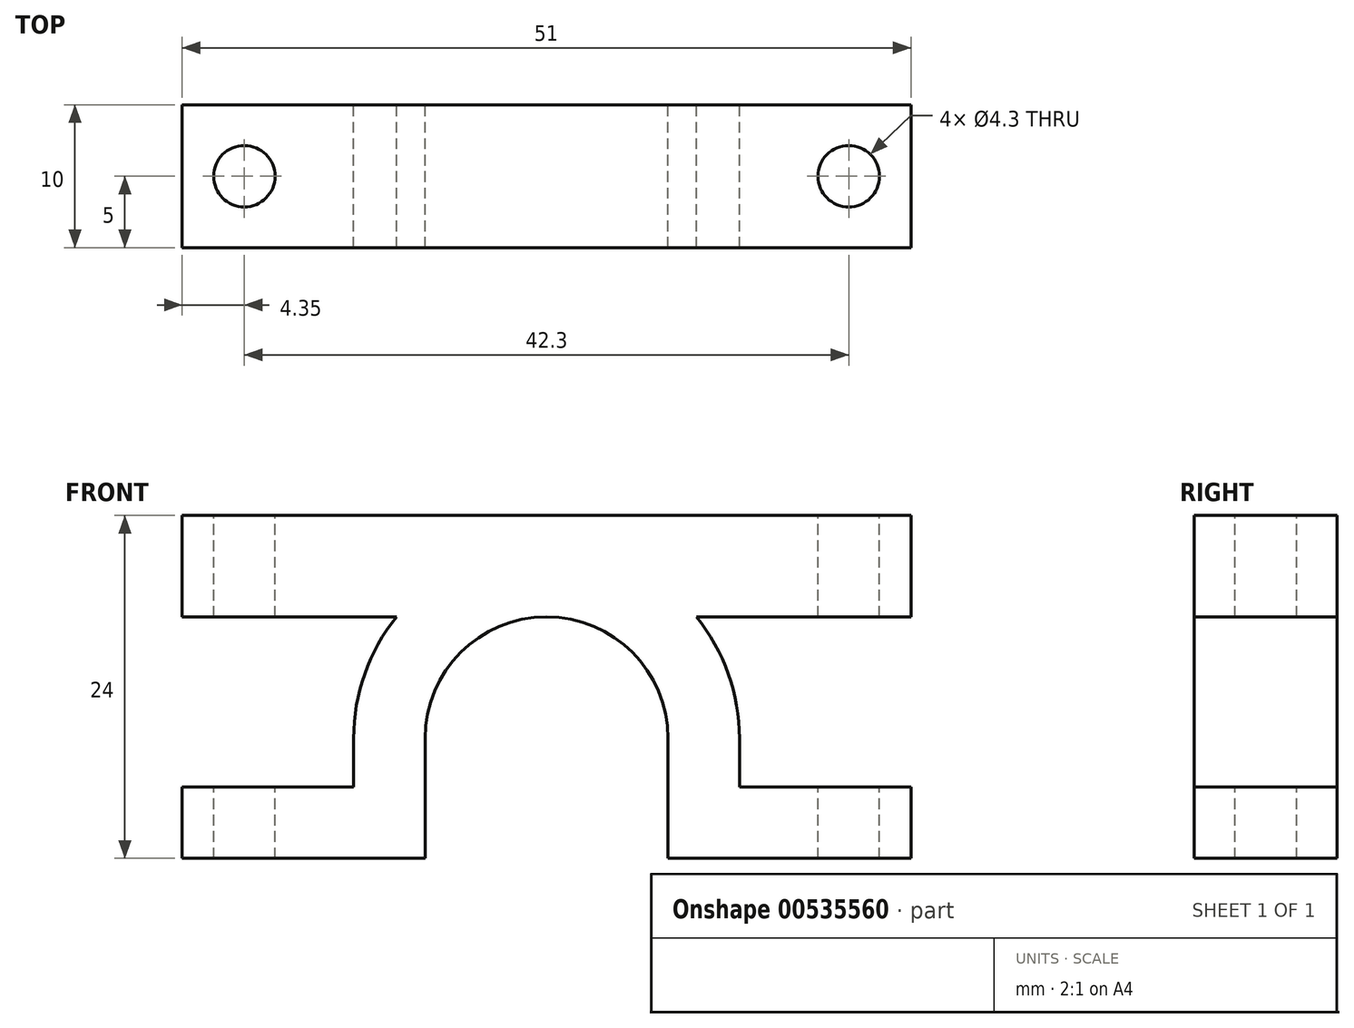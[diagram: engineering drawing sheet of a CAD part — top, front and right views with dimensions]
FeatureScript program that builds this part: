
annotation { "Feature Type Name" : "Feature", "Feature Type Description" : "" }
export const myFeature = defineFeature(function(context is Context, id is Id, definition is map)
    precondition{}
    {
        {
            var Q0;
            Q0=qCreatedBy(makeId("Front.planeOp"),FACE);
            var sketch = newSketch(context, id + "F0", { "sketchPlane" : qUnion([Q0])});
            skCircle(sketch, "E0", {"center": v(0, 0) * mm, "radius": 8.3 * mm});
            skSolve(sketch);
        }
        {
            var Q0;
            Q0=qCreatedBy(makeId("Front.planeOp"),FACE);
            var sketch = newSketch(context, id + "F1", { "sketchPlane" : qUnion([Q0])});
            skLineSegment(sketch, "E1", {"start": v(-25.5, -8.4) * mm, "end": v(-25.5, -3.4) * mm});
            skLineSegment(sketch, "E2", {"start": v(-25.5, -3.4) * mm, "end": v(-13.5, -3.4) * mm});
            skLineSegment(sketch, "E3", {"start": v(-8.5, 0) * mm, "end": v(-8.5, -8.4) * mm});
            skLineSegment(sketch, "E4", {"start": v(-25.5, -8.4) * mm, "end": v(-8.5, -8.4) * mm});
            skLineSegment(sketch, "E5.MirrorCS", {"start": v(8.5, 0) * mm, "end": v(8.5, -8.4) * mm});
            skLineSegment(sketch, "E6.MirrorCS", {"start": v(25.5, -3.4) * mm, "end": v(13.5, -3.4) * mm});
            skLineSegment(sketch, "E7.MirrorCS", {"start": v(25.5, -8.4) * mm, "end": v(25.5, -3.4) * mm});
            skLineSegment(sketch, "E8.MirrorCS", {"start": v(25.5, -8.4) * mm, "end": v(8.5, -8.4) * mm});
            skArc(sketch, "E9", {"start": v(8.5, 0) * mm, "mid": v(0, 8.5) * mm, "end": v(-8.5, 0) * mm});
            skLineSegment(sketch, "E10", {"start": v(-13.5, -3.4) * mm, "end": v(-13.5, 0) * mm});
            skLineSegment(sketch, "E11", {"start": v(13.5, -3.4) * mm, "end": v(13.5, 0) * mm});
            skArc(sketch, "E12", {"start": v(13.5, 0) * mm, "mid": v(0, 13.5) * mm, "end": v(-13.5, 0) * mm});
            skLineSegment(sketch, "E13.bottom", {"start": v(-25.5, 15.6) * mm, "end": v(25.5, 15.6) * mm});
            skLineSegment(sketch, "E13.top", {"start": v(-25.5, 8.5) * mm, "end": v(25.5, 8.5) * mm});
            skLineSegment(sketch, "E13.left", {"start": v(-25.5, 15.6) * mm, "end": v(-25.5, 8.5) * mm});
            skLineSegment(sketch, "E13.right", {"start": v(25.5, 15.6) * mm, "end": v(25.5, 8.5) * mm});
            skPoint(sketch, "E13.middle", {"position": v(0, 12.05) * mm});
            skSolve(sketch);
        }
        {
            var Q0;
            Q0 = qSketchRegion(id + "F1", true);
            extrude(context, id + "F2", {"entities" : qUnion([Q0]), "depth" : 10 * mm, "offsetDistance" : 25 * mm});
        }
        {
            var Q0;
            Q0=qCreatedBy(makeId("Top.planeOp"),FACE);
            var sketch = newSketch(context, id + "F3", { "sketchPlane" : qUnion([Q0])});
            skCircle(sketch, "E14", {"center": v(-21.15, -5) * mm, "radius": 2.15 * mm});
            skCircle(sketch, "E15", {"center": v(21.15, -5) * mm, "radius": 2.15 * mm});
            skSolve(sketch);
        }
        {
            var Q0;
            Q0 = qSketchRegion(id + "F3", true);
            extrude(context, id + "F4", {"entities" : qUnion([Q0]), "operationType" : NewBodyOperationType.REMOVE, "oppositeDirection" : true, "depth" : 50 * mm, "offsetDistance" : 25 * mm, "symmetric" : true});
        }
    });
